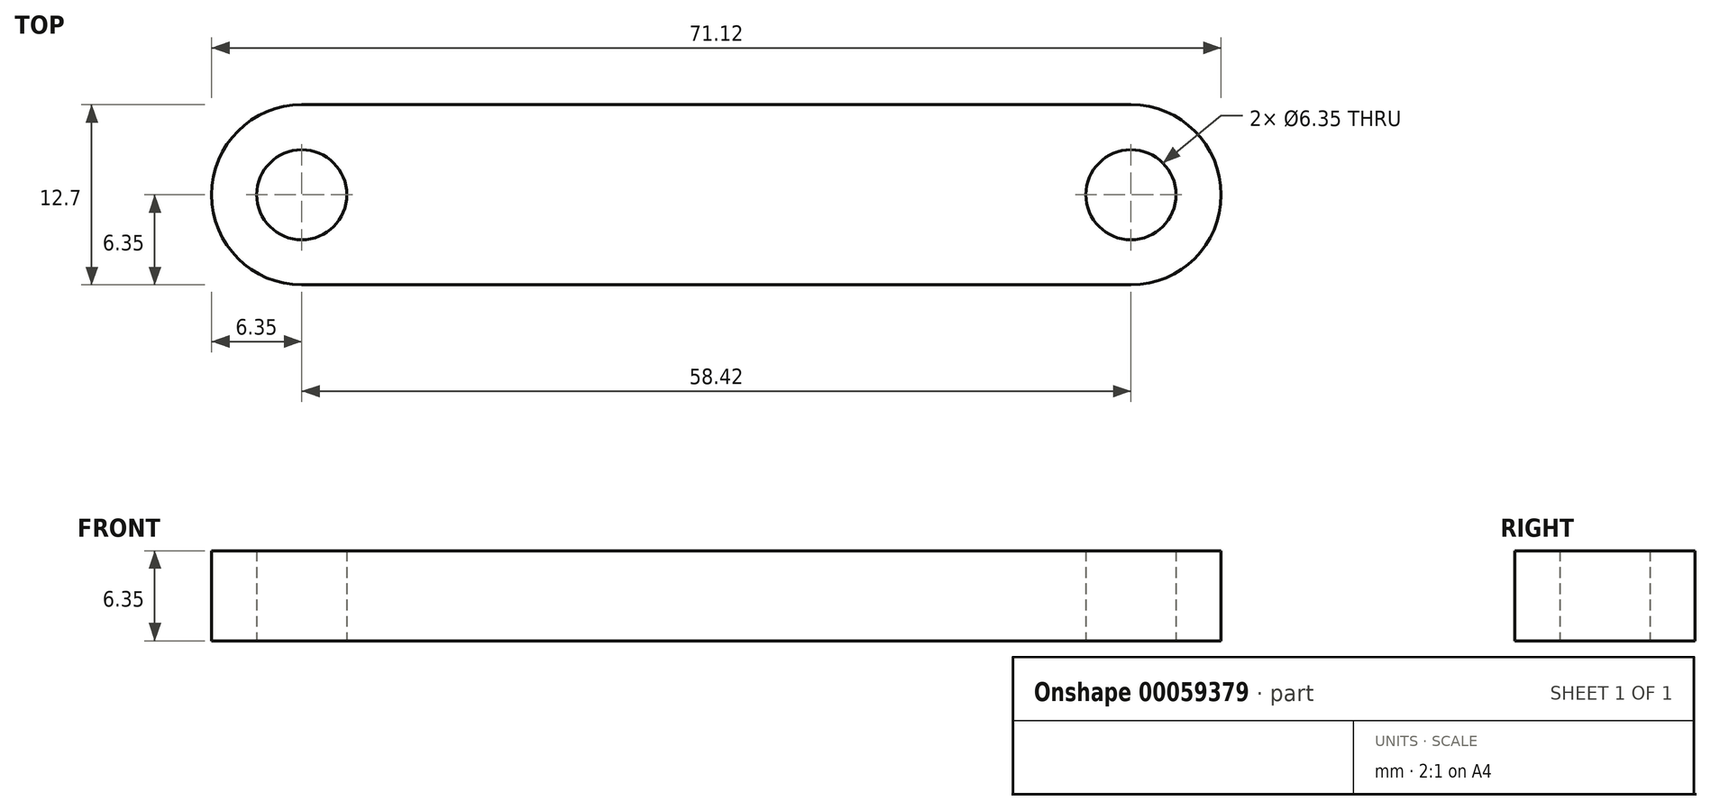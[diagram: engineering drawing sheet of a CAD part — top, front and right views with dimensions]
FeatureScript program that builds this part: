
annotation { "Feature Type Name" : "Feature", "Feature Type Description" : "" }
export const myFeature = defineFeature(function(context is Context, id is Id, definition is map)
    precondition{}
    {
        {
            var Q0;
            Q0=qCreatedBy(makeId("Top.planeOp"),FACE);
            var sketch = newSketch(context, id + "F0", { "sketchPlane" : qUnion([Q0])});
            skLineSegment(sketch, "E0.bottom", {"start": v(-29.21, 6.35) * mm, "end": v(29.2, 6.35) * mm});
            skLineSegment(sketch, "E0.top", {"start": v(-29.21, -6.35) * mm, "end": v(29.2, -6.35) * mm});
            skLineSegment(sketch, "E0.left", {"start": v(-29.21, 6.35) * mm, "end": v(-29.21, -6.35) * mm});
            skLineSegment(sketch, "E0.right", {"start": v(29.2, 6.35) * mm, "end": v(29.2, -6.35) * mm});
            skCircle(sketch, "E1", {"center": v(-29.21, 0) * mm, "radius": 6.35 * mm});
            skCircle(sketch, "E2", {"center": v(29.2, 0) * mm, "radius": 6.35 * mm});
            skCircle(sketch, "E3", {"center": v(29.2, 0) * mm, "radius": 3.18 * mm});
            skCircle(sketch, "E4", {"center": v(-29.21, 0) * mm, "radius": 3.18 * mm});
            skLineSegment(sketch, "E5", {"start": v(0, 0) * mm, "end": v(0, 55.19) * mm, "construction": true});
            skLineSegment(sketch, "E6", {"start": v(0, 0) * mm, "end": v(-65.33, 0) * mm, "construction": true});
            skSolve(sketch);
        }
        {
            var Q0;
            {var subQ0=sQuery(id+"F0.wireOp",EDGE,"E0.bottom");Q0=makeQuery(id+"F0.imprint","IMPRINT",FACE,{"disambiguationData":[TD([[makeQuery(id+"F0.imprint","IMPRINT",EDGE,{"derivedFrom":subQ0}),-1.0]])]});}
            var Q1;
            {var subQ1=sQuery(id+"F0.wireOp",EDGE,"E0.right");var subQ3=sQuery(id+"F0.wireOp",EDGE,"E3");var subQ4=makeQuery(id+"F0.imprint","INTERSECT",VERTEX,{"disambiguationData":[OD(0.0)],"derivedFrom":[subQ1,subQ3]});Q1=makeQuery(id+"F0.imprint","IMPRINT",FACE,{"disambiguationData":[TD([[makeQuery(id+"F0.imprint","IMPRINT",EDGE,{"disambiguationData":[TD([[subQ4,-1.0]])],"derivedFrom":subQ3}),-1.0]])]});}
            var Q2;
            {var subQ1=sQuery(id+"F0.wireOp",EDGE,"E0.right");var subQ3=sQuery(id+"F0.wireOp",EDGE,"E3");var subQ4=makeQuery(id+"F0.imprint","INTERSECT",VERTEX,{"disambiguationData":[OD(0.0)],"derivedFrom":[subQ1,subQ3]});Q2=makeQuery(id+"F0.imprint","IMPRINT",FACE,{"disambiguationData":[TD([[makeQuery(id+"F0.imprint","IMPRINT",EDGE,{"disambiguationData":[TD([[subQ4,1.0]])],"derivedFrom":subQ3}),-1.0]])]});}
            var Q3;
            {var subQ1=sQuery(id+"F0.wireOp",EDGE,"E0.left");var subQ3=sQuery(id+"F0.wireOp",EDGE,"E4");var subQ4=makeQuery(id+"F0.imprint","INTERSECT",VERTEX,{"disambiguationData":[OD(0.0)],"derivedFrom":[subQ1,subQ3]});Q3=makeQuery(id+"F0.imprint","IMPRINT",FACE,{"disambiguationData":[TD([[makeQuery(id+"F0.imprint","IMPRINT",EDGE,{"disambiguationData":[TD([[subQ4,-1.0]])],"derivedFrom":subQ3}),-1.0]])]});}
            var Q4;
            {var subQ1=sQuery(id+"F0.wireOp",EDGE,"E0.left");var subQ3=sQuery(id+"F0.wireOp",EDGE,"E4");var subQ4=makeQuery(id+"F0.imprint","INTERSECT",VERTEX,{"disambiguationData":[OD(0.0)],"derivedFrom":[subQ1,subQ3]});Q4=makeQuery(id+"F0.imprint","IMPRINT",FACE,{"disambiguationData":[TD([[makeQuery(id+"F0.imprint","IMPRINT",EDGE,{"disambiguationData":[TD([[subQ4,1.0]])],"derivedFrom":subQ3}),-1.0]])]});}
            extrude(context, id + "F1", {"entities" : qUnion([Q0, Q1, Q2, Q3, Q4]), "depth" : 6.35 * mm});
        }
    });
